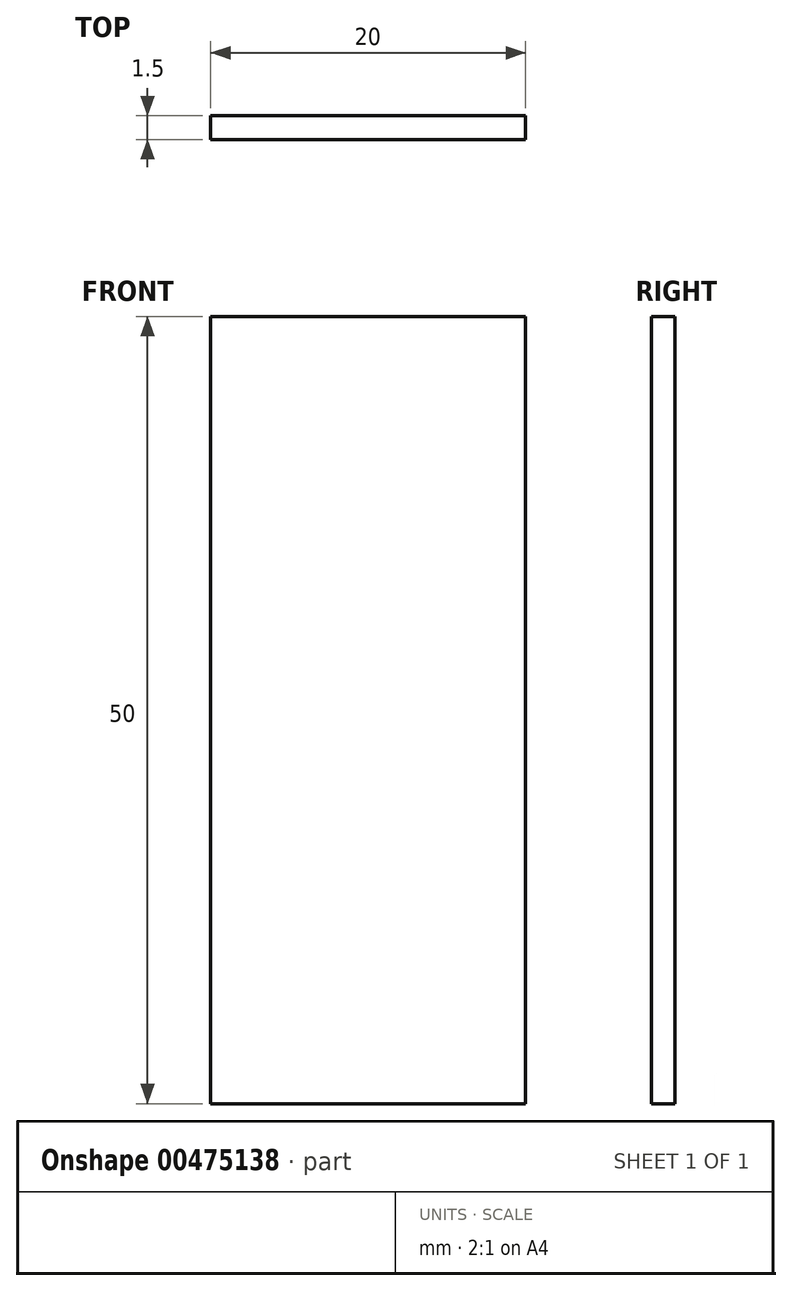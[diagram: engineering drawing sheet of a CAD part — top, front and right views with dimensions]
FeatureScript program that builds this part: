
annotation { "Feature Type Name" : "Feature", "Feature Type Description" : "" }
export const myFeature = defineFeature(function(context is Context, id is Id, definition is map)
    precondition{}
    {
        {
            var Q0;
            Q0=qCreatedBy(makeId("Front.planeOp"),FACE);
            var sketch = newSketch(context, id + "F0", { "sketchPlane" : qUnion([Q0])});
            skLineSegment(sketch, "E0.bottom", {"start": v(0, 0) * mm, "end": v(0, 0) * mm});
            skLineSegment(sketch, "E0.top", {"start": v(0, 0) * mm, "end": v(0, 0) * mm});
            skLineSegment(sketch, "E0.left", {"start": v(0, 0) * mm, "end": v(0, 0) * mm});
            skLineSegment(sketch, "E0.right", {"start": v(0, 0) * mm, "end": v(0, 0) * mm});
            skPoint(sketch, "E0.middle", {"position": v(0, 0) * mm});
            skLineSegment(sketch, "E1.bottom", {"start": v(10, -25) * mm, "end": v(-10, -25) * mm});
            skLineSegment(sketch, "E1.top", {"start": v(10, 25) * mm, "end": v(-10, 25) * mm});
            skLineSegment(sketch, "E1.left", {"start": v(10, -25) * mm, "end": v(10, 25) * mm});
            skLineSegment(sketch, "E1.right", {"start": v(-10, -25) * mm, "end": v(-10, 25) * mm});
            skSolve(sketch);
        }
        {
            var Q0;
            Q0=makeQuery(id+"F0.imprint","IMPRINT",FACE,{"disambiguationData":[TD([[makeQuery(id+"F0.imprint","IMPRINT",EDGE,{"derivedFrom":sQuery(id+"F0.wireOp",EDGE,"E1.bottom")}),-1.0]])]});
            extrude(context, id + "F1", {"entities" : qUnion([Q0]), "depth" : 1.5 * mm});
        }
    });
